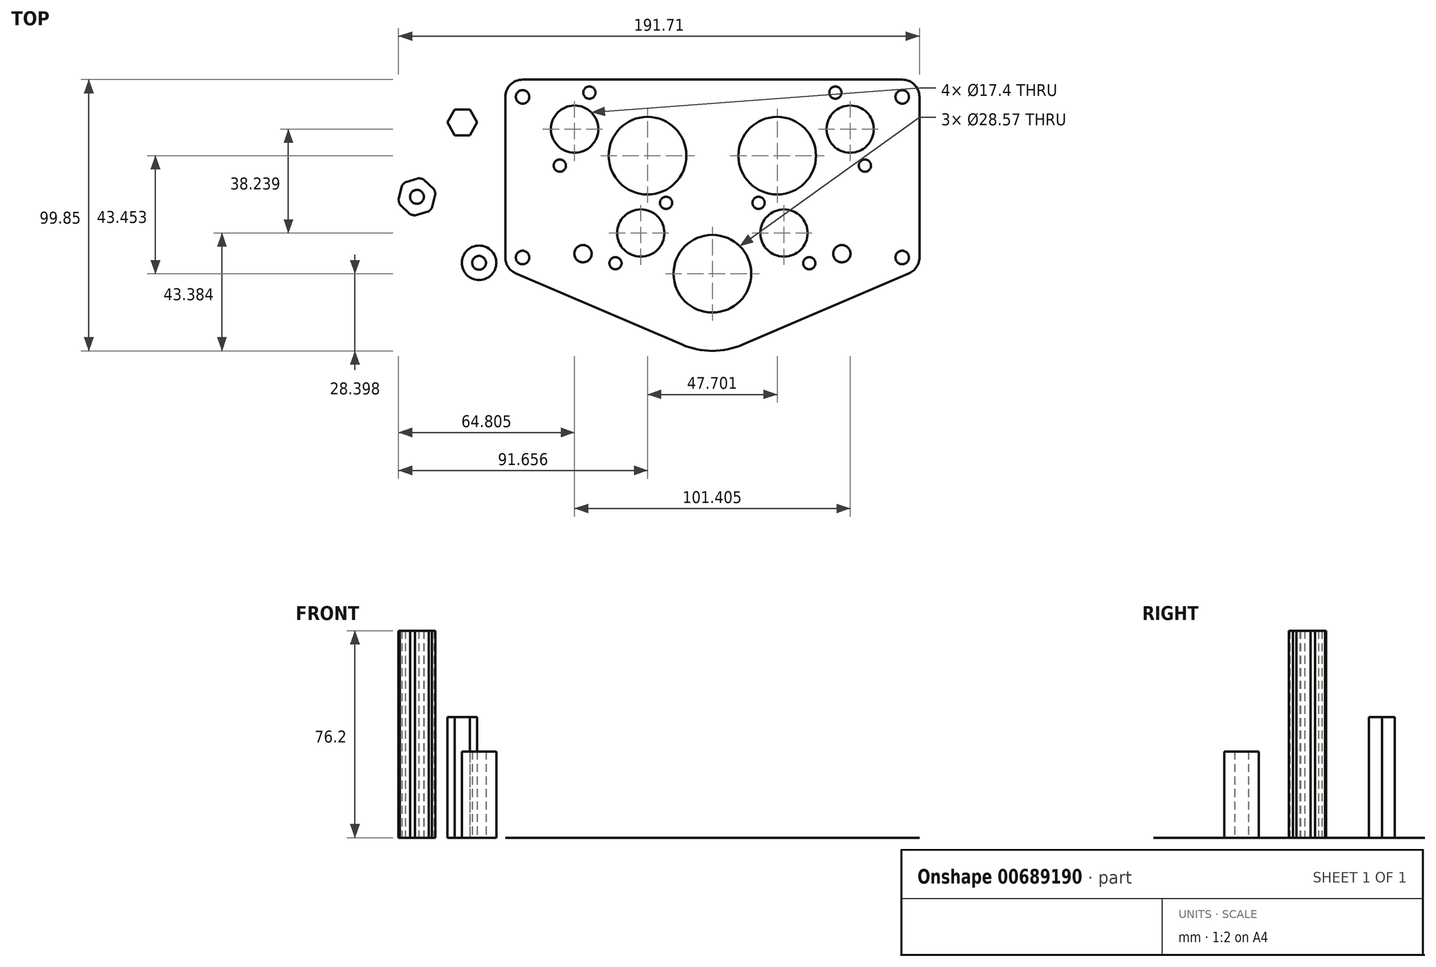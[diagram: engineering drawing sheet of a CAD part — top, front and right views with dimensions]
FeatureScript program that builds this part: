
annotation { "Feature Type Name" : "Feature", "Feature Type Description" : "" }
export const myFeature = defineFeature(function(context is Context, id is Id, definition is map)
    precondition{}
    {
        {
            var Q0;
            Q0=qCreatedBy(makeId("Top.planeOp"),FACE);
            var sketch = newSketch(context, id + "F0", { "sketchPlane" : qUnion([Q0])});
            skCircle(sketch, "E0", {"center": v(-197.76, 76.3) * mm, "radius": 8.7 * mm});
            skCircle(sketch, "E1", {"center": v(-173.4, 38.05) * mm, "radius": 8.7 * mm});
            skCircle(sketch, "E2", {"center": v(-197.76, 76.3) * mm, "radius": 4.76 * mm, "construction": true});
            skCircle(sketch, "E3", {"center": v(-173.4, 38.05) * mm, "radius": 4.76 * mm, "construction": true});
            skCircle(sketch, "E4", {"center": v(-170.9, 66.52) * mm, "radius": 23.81 * mm, "construction": true});
            skCircle(sketch, "E5", {"center": v(-170.9, 66.52) * mm, "radius": 14.29 * mm});
            skCircle(sketch, "E6", {"center": v(-170.9, 66.52) * mm, "radius": 11.43 * mm, "construction": true});
            skLineSegment(sketch, "E7", {"start": v(-170.9, 66.52) * mm, "end": v(-194.72, 66.52) * mm, "construction": true});
            skLineSegment(sketch, "E8", {"start": v(-197.76, 76.3) * mm, "end": v(-170.9, 66.52) * mm, "construction": true});
            skCircle(sketch, "E9", {"center": v(-197.76, 76.3) * mm, "radius": 22.23 * mm, "construction": true});
            skCircle(sketch, "E10", {"center": v(-173.4, 38.05) * mm, "radius": 22.23 * mm, "construction": true});
            skLineSegment(sketch, "E11", {"start": v(-147.05, 94.52) * mm, "end": v(-147.05, -5.33) * mm, "construction": true});
            skCircle(sketch, "E12.MirrorC", {"center": v(-96.35, 76.3) * mm, "radius": 4.76 * mm, "construction": true});
            skCircle(sketch, "E13.MirrorC", {"center": v(-120.71, 38.05) * mm, "radius": 4.76 * mm, "construction": true});
            skCircle(sketch, "E14.MirrorC", {"center": v(-120.71, 38.05) * mm, "radius": 22.23 * mm, "construction": true});
            skLineSegment(sketch, "E15.MirrorCS", {"start": v(-120.71, 38.05) * mm, "end": v(-123.2, 66.52) * mm, "construction": true});
            skCircle(sketch, "E16.MirrorC", {"center": v(-123.2, 66.52) * mm, "radius": 23.81 * mm, "construction": true});
            skCircle(sketch, "E17.MirrorC", {"center": v(-123.2, 66.52) * mm, "radius": 14.29 * mm});
            skCircle(sketch, "E18.MirrorC", {"center": v(-120.71, 38.05) * mm, "radius": 8.7 * mm});
            skCircle(sketch, "E19.MirrorC", {"center": v(-96.35, 76.3) * mm, "radius": 22.23 * mm, "construction": true});
            skLineSegment(sketch, "E20.MirrorCS", {"start": v(-123.2, 66.52) * mm, "end": v(-99.39, 66.52) * mm, "construction": true});
            skLineSegment(sketch, "E21.MirrorCS", {"start": v(-96.35, 76.3) * mm, "end": v(-123.2, 66.52) * mm, "construction": true});
            skCircle(sketch, "E22.MirrorC", {"center": v(-96.35, 76.3) * mm, "radius": 8.7 * mm});
            skCircle(sketch, "E23.MirrorC", {"center": v(-123.2, 66.52) * mm, "radius": 11.43 * mm, "construction": true});
            skLineSegment(sketch, "E24.bottom", {"start": v(-216.9, 94.52) * mm, "end": v(-77.2, 94.52) * mm});
            skLineSegment(sketch, "E24.left", {"start": v(-223.25, 88.17) * mm, "end": v(-223.25, 29.04) * mm});
            skLineSegment(sketch, "E24.right", {"start": v(-70.85, 88.17) * mm, "end": v(-70.85, 29.04) * mm});
            skPoint(sketch, "E24.middle", {"position": v(-147.05, 54.57) * mm});
            skCircle(sketch, "E25", {"center": v(-147.05, 23.07) * mm, "radius": 14.29 * mm});
            skCircle(sketch, "E26", {"center": v(-147.05, 23.07) * mm, "radius": 38.14 * mm, "construction": true});
            skArc(sketch, "E27", {"start": v(-158.25, -3.03) * mm, "mid": v(-147.05, -5.33) * mm, "end": v(-135.86, -3.03) * mm});
            skLineSegment(sketch, "E28", {"start": v(-158.25, -3.03) * mm, "end": v(-219.4, 23.2) * mm});
            skLineSegment(sketch, "E29", {"start": v(-135.86, -3.03) * mm, "end": v(-74.7, 23.2) * mm});
            skCircle(sketch, "E30", {"center": v(-216.9, 88.17) * mm, "radius": 2.49 * mm});
            skLineSegment(sketch, "E31", {"start": v(-216.9, 88.17) * mm, "end": v(-223.25, 88.17) * mm, "construction": true});
            skLineSegment(sketch, "E32", {"start": v(-216.9, 88.17) * mm, "end": v(-216.9, 94.52) * mm, "construction": true});
            skCircle(sketch, "E33.MirrorC", {"center": v(-77.2, 88.17) * mm, "radius": 2.49 * mm});
            skCircle(sketch, "E34", {"center": v(-216.9, 29.04) * mm, "radius": 2.49 * mm});
            skCircle(sketch, "E35.MirrorC", {"center": v(-77.2, 29.04) * mm, "radius": 2.49 * mm});
            skLineSegment(sketch, "E36", {"start": v(-164.07, 49.16) * mm, "end": v(-182.72, 26.94) * mm, "construction": true});
            skCircle(sketch, "E37", {"center": v(-164.07, 49.16) * mm, "radius": 2.25 * mm});
            skCircle(sketch, "E38", {"center": v(-182.72, 26.94) * mm, "radius": 2.25 * mm});
            skLineSegment(sketch, "E39", {"start": v(-192.32, 89.74) * mm, "end": v(-203.19, 62.85) * mm, "construction": true});
            skCircle(sketch, "E40", {"center": v(-203.19, 62.85) * mm, "radius": 2.25 * mm});
            skCircle(sketch, "E41", {"center": v(-192.32, 89.74) * mm, "radius": 2.25 * mm});
            skCircle(sketch, "E42.MirrorC", {"center": v(-90.92, 62.85) * mm, "radius": 2.25 * mm});
            skCircle(sketch, "E43.MirrorC", {"center": v(-101.78, 89.74) * mm, "radius": 2.25 * mm});
            skCircle(sketch, "E44.MirrorC", {"center": v(-111.39, 26.94) * mm, "radius": 2.25 * mm});
            skCircle(sketch, "E45.MirrorC", {"center": v(-130.03, 49.16) * mm, "radius": 2.25 * mm});
            skLineSegment(sketch, "E46", {"start": v(-194.68, 30.44) * mm, "end": v(-99.43, 30.44) * mm, "construction": true});
            skPoint(sketch, "E47", {"position": v(-147.05, 30.44) * mm});
            skCircle(sketch, "E48", {"center": v(-194.68, 30.44) * mm, "radius": 3.18 * mm});
            skCircle(sketch, "E49", {"center": v(-99.43, 30.44) * mm, "radius": 3.18 * mm});
            skLineSegment(sketch, "E50", {"start": v(-173.4, 38.05) * mm, "end": v(-170.9, 66.52) * mm, "construction": true});
            skArc(sketch, "E51", {"start": v(-216.9, 94.52) * mm, "mid": v(-221.4, 92.66) * mm, "end": v(-223.25, 88.17) * mm});
            skPoint(sketch, "E52.orphan", {"position": v(-223.25, 94.52) * mm});
            skArc(sketch, "E53.MirrorCS", {"start": v(-77.2, 94.52) * mm, "mid": v(-72.71, 92.66) * mm, "end": v(-70.85, 88.17) * mm});
            skArc(sketch, "E54", {"start": v(-223.25, 29.04) * mm, "mid": v(-222.2, 25.54) * mm, "end": v(-219.4, 23.2) * mm});
            skArc(sketch, "E55.MirrorCS", {"start": v(-70.85, 29.04) * mm, "mid": v(-71.9, 25.54) * mm, "end": v(-74.7, 23.2) * mm});
            skSolve(sketch);
        }
        {
            var Q0;
            Q0=makeQuery(id+"F0.imprint","IMPRINT",FACE,{"disambiguationData":[TD([[makeQuery(id+"F0.imprint","IMPRINT",EDGE,{"derivedFrom":sQuery(id+"F0.wireOp",EDGE,"E0")}),-1.0]])]});
            extrude(context, id + "F1", {"entities" : qUnion([Q0]), "depth" : 1 / 101.6 * mm, "offsetDistance" : 25.4 * mm});
        }
        {
            var Q0;
            Q0=makeQuery(id+"F1.opExtrude","CAP_FACE",FACE,{"disambiguationData":[OSD([sQuery(id+"F0.wireOp",EDGE,"E0"),sQuery(id+"F0.wireOp",EDGE,"E1"),sQuery(id+"F0.wireOp",EDGE,"E5"),sQuery(id+"F0.wireOp",EDGE,"E17.MirrorC"),sQuery(id+"F0.wireOp",EDGE,"E18.MirrorC"),sQuery(id+"F0.wireOp",EDGE,"E22.MirrorC"),sQuery(id+"F0.wireOp",EDGE,"E24.bottom"),sQuery(id+"F0.wireOp",EDGE,"E24.left"),sQuery(id+"F0.wireOp",EDGE,"E24.right"),sQuery(id+"F0.wireOp",EDGE,"E25"),sQuery(id+"F0.wireOp",EDGE,"E27"),sQuery(id+"F0.wireOp",EDGE,"E28"),sQuery(id+"F0.wireOp",EDGE,"E29"),sQuery(id+"F0.wireOp",EDGE,"E30"),sQuery(id+"F0.wireOp",EDGE,"E33.MirrorC"),sQuery(id+"F0.wireOp",EDGE,"E34"),sQuery(id+"F0.wireOp",EDGE,"E35.MirrorC"),sQuery(id+"F0.wireOp",EDGE,"E37"),sQuery(id+"F0.wireOp",EDGE,"E38"),sQuery(id+"F0.wireOp",EDGE,"E40"),sQuery(id+"F0.wireOp",EDGE,"E41"),sQuery(id+"F0.wireOp",EDGE,"E42.MirrorC"),sQuery(id+"F0.wireOp",EDGE,"E43.MirrorC"),sQuery(id+"F0.wireOp",EDGE,"E44.MirrorC"),sQuery(id+"F0.wireOp",EDGE,"E45.MirrorC"),sQuery(id+"F0.wireOp",EDGE,"E48"),sQuery(id+"F0.wireOp",EDGE,"E49"),sQuery(id+"F0.wireOp",EDGE,"E51"),sQuery(id+"F0.wireOp",EDGE,"E53.MirrorCS"),sQuery(id+"F0.wireOp",EDGE,"E54"),sQuery(id+"F0.wireOp",EDGE,"E55.MirrorCS")])],"isStart":false});
            var sketch = newSketch(context, id + "F2", { "sketchPlane" : qUnion([Q0])});
            skCircle(sketch, "E56.0", {"center": v(-197.76, 76.3) * mm, "radius": 8.7 * mm});
            skCircle(sketch, "E56.1", {"center": v(-96.35, 76.3) * mm, "radius": 8.7 * mm});
            skLineSegment(sketch, "E56.2", {"start": v(-216.9, 94.52) * mm, "end": v(-77.2, 94.52) * mm});
            skCircle(sketch, "E56.3", {"center": v(-147.05, 23.07) * mm, "radius": 14.29 * mm});
            skCircle(sketch, "E56.4", {"center": v(-170.9, 66.52) * mm, "radius": 14.29 * mm});
            skLineSegment(sketch, "E56.5", {"start": v(-70.85, 88.17) * mm, "end": v(-70.85, 29.04) * mm});
            skArc(sketch, "E56.6", {"start": v(-158.25, -3.03) * mm, "mid": v(-147.05, -5.33) * mm, "end": v(-135.86, -3.03) * mm});
            skLineSegment(sketch, "E56.7", {"start": v(-223.25, 88.17) * mm, "end": v(-223.25, 29.04) * mm});
            skLineSegment(sketch, "E56.8", {"start": v(-158.25, -3.03) * mm, "end": v(-219.4, 23.2) * mm});
            skArc(sketch, "E56.9", {"start": v(-216.9, 94.52) * mm, "mid": v(-221.4, 92.66) * mm, "end": v(-223.25, 88.17) * mm});
            skCircle(sketch, "E56.10", {"center": v(-123.2, 66.52) * mm, "radius": 14.29 * mm});
            skCircle(sketch, "E56.11", {"center": v(-173.4, 38.05) * mm, "radius": 8.7 * mm});
            skCircle(sketch, "E56.12", {"center": v(-120.71, 38.05) * mm, "radius": 8.7 * mm});
            skArc(sketch, "E56.13", {"start": v(-77.2, 94.52) * mm, "mid": v(-72.71, 92.66) * mm, "end": v(-70.85, 88.17) * mm});
            skLineSegment(sketch, "E56.14", {"start": v(-135.86, -3.03) * mm, "end": v(-74.7, 23.2) * mm});
            skCircle(sketch, "E57.0", {"center": v(-194.68, 30.44) * mm, "radius": 3.18 * mm});
            skCircle(sketch, "E58.0", {"center": v(-216.9, 29.04) * mm, "radius": 2.49 * mm});
            skCircle(sketch, "E59.0", {"center": v(-182.72, 26.94) * mm, "radius": 2.25 * mm});
            skCircle(sketch, "E60.0", {"center": v(-164.07, 49.16) * mm, "radius": 2.25 * mm});
            skCircle(sketch, "E61.0", {"center": v(-203.19, 62.85) * mm, "radius": 2.25 * mm});
            skCircle(sketch, "E62.0", {"center": v(-192.32, 89.74) * mm, "radius": 2.25 * mm});
            skCircle(sketch, "E63.0", {"center": v(-101.78, 89.74) * mm, "radius": 2.25 * mm});
            skCircle(sketch, "E64.0", {"center": v(-90.92, 62.85) * mm, "radius": 2.25 * mm});
            skCircle(sketch, "E65.0", {"center": v(-111.39, 26.94) * mm, "radius": 2.25 * mm});
            skCircle(sketch, "E66.0", {"center": v(-130.03, 49.16) * mm, "radius": 2.25 * mm});
            skCircle(sketch, "E67.0", {"center": v(-77.2, 29.04) * mm, "radius": 2.49 * mm});
            skCircle(sketch, "E68.0", {"center": v(-99.43, 30.44) * mm, "radius": 3.18 * mm});
            skLineSegment(sketch, "E69", {"start": v(-147.05, -5.33) * mm, "end": v(-147.05, 94.52) * mm});
            skSolve(sketch);
        }
        {
            var Q0;
            Q0=qCreatedBy(makeId("Top.planeOp"),FACE);
            var sketch = newSketch(context, id + "F3", { "sketchPlane" : qUnion([Q0])});
            skCircle(sketch, "E70", {"center": v(-232.9, 27.08) * mm, "radius": 6.35 * mm});
            skCircle(sketch, "E71", {"center": v(-232.9, 27.08) * mm, "radius": 2.54 * mm});
            skSolve(sketch);
        }
        {
            var Q0;
            Q0=makeQuery(id+"F3.imprint","IMPRINT",FACE,{"disambiguationData":[TD([[makeQuery(id+"F3.imprint","IMPRINT",EDGE,{"derivedFrom":sQuery(id+"F3.wireOp",EDGE,"E70")}),1.0]])]});
            extrude(context, id + "F4", {"entities" : qUnion([Q0]), "depth" : 31.75 * mm, "offsetDistance" : 25.4 * mm});
        }
        {
            var Q0;
            Q0=qCreatedBy(makeId("Top.planeOp"),FACE);
            var sketch = newSketch(context, id + "F5", { "sketchPlane" : qUnion([Q0])});
            skCircle(sketch, "E72.cCircle", {"center": v(-239.1, 78.76) * mm, "radius": 4.76 * mm, "construction": true});
            skLineSegment(sketch, "E72.0", {"start": v(-236.34, 74) * mm, "end": v(-241.84, 74) * mm});
            skLineSegment(sketch, "E72.1", {"start": v(-241.84, 74) * mm, "end": v(-244.59, 78.76) * mm});
            skLineSegment(sketch, "E72.2", {"start": v(-244.59, 78.76) * mm, "end": v(-241.84, 83.52) * mm});
            skLineSegment(sketch, "E72.3", {"start": v(-241.84, 83.52) * mm, "end": v(-236.34, 83.52) * mm});
            skLineSegment(sketch, "E72.4", {"start": v(-236.34, 83.52) * mm, "end": v(-233.6, 78.76) * mm});
            skLineSegment(sketch, "E72.5", {"start": v(-233.6, 78.76) * mm, "end": v(-236.34, 74) * mm});
            skPoint(sketch, "E72.0.midPoint", {"position": v(-239.1, 74) * mm});
            skSolve(sketch);
        }
        {
            var Q0;
            Q0=makeQuery(id+"F5.imprint","IMPRINT",FACE,{"disambiguationData":[TD([[makeQuery(id+"F5.imprint","IMPRINT",EDGE,{"derivedFrom":sQuery(id+"F5.wireOp",EDGE,"E72.0")}),-1.0]])]});
            extrude(context, id + "F6", {"entities" : qUnion([Q0]), "depth" : 44.45 * mm, "offsetDistance" : 25.4 * mm});
        }
        {
            var Q0;
            Q0=qCreatedBy(makeId("Top.planeOp"),FACE);
            var sketch = newSketch(context, id + "F7", { "sketchPlane" : qUnion([Q0])});
            skCircle(sketch, "E73", {"center": v(-255.77, 51.38) * mm, "radius": 2.55 * mm});
            skCircle(sketch, "E74.cCircle", {"center": v(-255.77, 51.38) * mm, "radius": 6.35 * mm, "construction": true});
            skLineSegment(sketch, "E74.0", {"start": v(-251.43, 46.04) * mm, "end": v(-256.5, 44.54) * mm});
            skLineSegment(sketch, "E74.1", {"start": v(-258.22, 44.95) * mm, "end": v(-262.05, 48.58) * mm});
            skLineSegment(sketch, "E74.2", {"start": v(-262.56, 50.3) * mm, "end": v(-261.33, 55.42) * mm});
            skLineSegment(sketch, "E74.3", {"start": v(-260.1, 56.71) * mm, "end": v(-255.04, 58.21) * mm});
            skLineSegment(sketch, "E74.4", {"start": v(-253.3, 57.8) * mm, "end": v(-249.48, 54.17) * mm});
            skLineSegment(sketch, "E74.5", {"start": v(-248.98, 52.46) * mm, "end": v(-250.2, 47.33) * mm});
            skPoint(sketch, "E74.0.midPoint", {"position": v(-253.96, 45.29) * mm});
            skArc(sketch, "E75", {"start": v(-258.22, 44.95) * mm, "mid": v(-257.37, 44.69) * mm, "end": v(-256.5, 44.54) * mm});
            skPoint(sketch, "E76.orphan", {"position": v(-257.48, 44.25) * mm});
            skPoint(sketch, "E77.orphan", {"position": v(-262.8, 49.3) * mm});
            skArc(sketch, "E78.trimOffspring", {"start": v(-262.56, 50.3) * mm, "mid": v(-262.36, 49.42) * mm, "end": v(-262.05, 48.58) * mm});
            skPoint(sketch, "E79.orphan", {"position": v(-261.09, 56.42) * mm});
            skArc(sketch, "E80.trimOffspring", {"start": v(-260.1, 56.71) * mm, "mid": v(-260.75, 56.1) * mm, "end": v(-261.33, 55.42) * mm});
            skPoint(sketch, "E81.orphan", {"position": v(-254.06, 58.5) * mm});
            skArc(sketch, "E82.trimOffspring", {"start": v(-253.3, 57.8) * mm, "mid": v(-254.16, 58.06) * mm, "end": v(-255.04, 58.21) * mm});
            skPoint(sketch, "E83.orphan", {"position": v(-248.74, 53.46) * mm});
            skArc(sketch, "E84.trimOffspring", {"start": v(-248.98, 52.46) * mm, "mid": v(-249.17, 53.33) * mm, "end": v(-249.48, 54.17) * mm});
            skPoint(sketch, "E85.orphan", {"position": v(-250.45, 46.33) * mm});
            skArc(sketch, "E86.trimOffspring", {"start": v(-251.43, 46.04) * mm, "mid": v(-250.78, 46.64) * mm, "end": v(-250.2, 47.33) * mm});
            skSolve(sketch);
        }
        {
            var Q0;
            Q0=makeQuery(id+"F7.imprint","IMPRINT",FACE,{"disambiguationData":[TD([[makeQuery(id+"F7.imprint","IMPRINT",EDGE,{"derivedFrom":sQuery(id+"F7.wireOp",EDGE,"E73")}),-1.0]])]});
            extrude(context, id + "F8", {"entities" : qUnion([Q0]), "depth" : 76.2 * mm, "offsetDistance" : 25.4 * mm});
        }
    });
